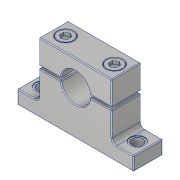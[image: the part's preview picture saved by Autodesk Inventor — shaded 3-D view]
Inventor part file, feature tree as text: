
AUTODESK INVENTOR PART (.ipt)
format: ipt  version: 2019.4 (Build 234330000, 330)  size: 289,792 bytes
history: native  units: in
note: dims shown in document units (in); Inventor stores cm internally (conversion verified against a paired STEP export)
features: fillet x2, mirror x1, other x1
ambient origin geometry x8: Origin, YZ Plane, XZ Plane, XY Plane, X Axis, Y Axis, Z Axis, Center Point
bodies: Solid1 (feature_tree), Solid2 (feature_tree), Solid3 (feature_tree), Solid4 (feature_tree)
feature tree (4):
  fillet  "Fillet3"  [1 undecoded]
  fillet  "Fillet1"  [1 undecoded]
  mirror  "Mirror1"
  other  "Cut-Extrude6"
note: 2 required parameter values undecoded (feature->parameter linkage not recoverable at this tier; creation-order binding heuristic only, values carry confidence <= 0.55)
